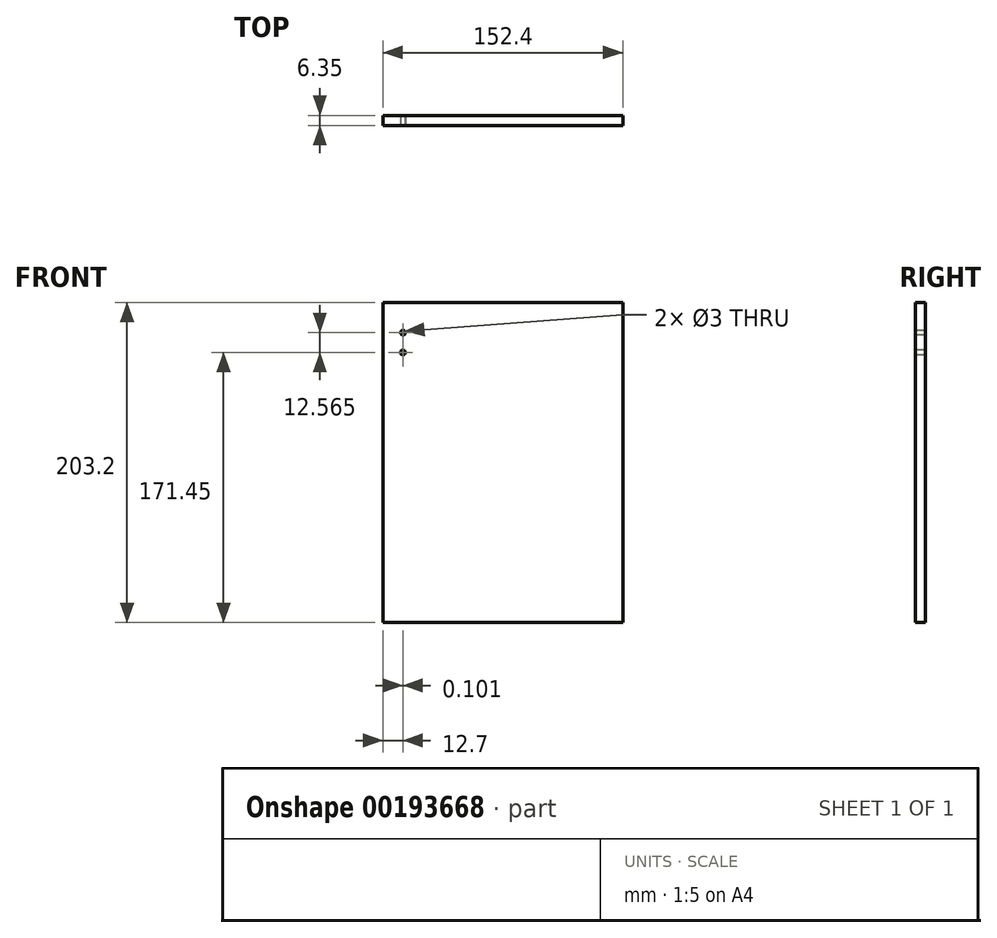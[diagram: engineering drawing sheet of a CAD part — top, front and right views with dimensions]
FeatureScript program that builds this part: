
annotation { "Feature Type Name" : "Feature", "Feature Type Description" : "" }
export const myFeature = defineFeature(function(context is Context, id is Id, definition is map)
    precondition{}
    {
        {
            var Q0;
            Q0=qCreatedBy(makeId("Front.planeOp"),FACE);
            var sketch = newSketch(context, id + "F0", { "sketchPlane" : qUnion([Q0])});
            skLineSegment(sketch, "E0.bottom", {"start": v(-76.2, -101.6) * mm, "end": v(76.2, -101.6) * mm});
            skLineSegment(sketch, "E0.top", {"start": v(-76.2, 101.6) * mm, "end": v(76.2, 101.6) * mm});
            skLineSegment(sketch, "E0.left", {"start": v(-76.2, -101.6) * mm, "end": v(-76.2, 101.6) * mm});
            skLineSegment(sketch, "E0.right", {"start": v(76.2, -101.6) * mm, "end": v(76.2, 101.6) * mm});
            skPoint(sketch, "E0.middle", {"position": v(0, 0) * mm});
            skSolve(sketch);
        }
        {
            var Q0;
            Q0=makeQuery(id+"F0.imprint","IMPRINT",FACE,{"disambiguationData":[TD([[makeQuery(id+"F0.imprint","IMPRINT",EDGE,{"derivedFrom":sQuery(id+"F0.wireOp",EDGE,"E0.bottom")}),1.0]])]});
            extrude(context, id + "F1", {"entities" : qUnion([Q0]), "oppositeDirection" : true, "depth" : 6.35 * mm});
        }
        {
            var Q0;
            Q0=makeQuery(id+"F1.opExtrude","CAP_FACE",FACE,{"disambiguationData":[OSD([sQuery(id+"F0.wireOp",EDGE,"E0.bottom"),sQuery(id+"F0.wireOp",EDGE,"E0.top"),sQuery(id+"F0.wireOp",EDGE,"E0.left"),sQuery(id+"F0.wireOp",EDGE,"E0.right")])],"isStart":true});
            var sketch = newSketch(context, id + "F2", { "sketchPlane" : qUnion([Q0])});
            skLineSegment(sketch, "E1", {"start": v(-63.5, 101.6) * mm, "end": v(-63.5, 82.55) * mm});
            skLineSegment(sketch, "E2", {"start": v(-63.5, 82.55) * mm, "end": v(-63.5, 69.85) * mm});
            skCircle(sketch, "E3", {"center": v(-63.4, 82.41) * mm, "radius": 1.5 * mm});
            skCircle(sketch, "E4", {"center": v(-63.5, 69.85) * mm, "radius": 1.5 * mm});
            skSolve(sketch);
        }
        {
            var Q0;
            {var subQ0=sQuery(id+"F2.wireOp",EDGE,"E2");var subQ1=sQuery(id+"F2.wireOp",EDGE,"E1");var subQ2=makeQuery(id+"F2.imprint","INTERSECT",VERTEX,{"derivedFrom":[subQ1,subQ0]});Q0=makeQuery(id+"F2.imprint","IMPRINT",FACE,{"disambiguationData":[TD([[makeQuery(id+"F2.imprint","IMPRINT",EDGE,{"disambiguationData":[TD([[subQ2,1.0]])],"derivedFrom":subQ1}),-1.0]])]});}
            var Q1;
            Q1=makeQuery(id+"F2.imprint","IMPRINT",FACE,{"disambiguationData":[TD([[makeQuery(id+"F2.imprint","IMPRINT",EDGE,{"derivedFrom":sQuery(id+"F2.wireOp",EDGE,"E4")}),1.0]])]});
            var Q2;
            {var subQ0=sQuery(id+"F2.wireOp",EDGE,"E2");var subQ1=sQuery(id+"F2.wireOp",EDGE,"E1");var subQ2=makeQuery(id+"F2.imprint","INTERSECT",VERTEX,{"derivedFrom":[subQ1,subQ0]});Q2=makeQuery(id+"F2.imprint","IMPRINT",FACE,{"disambiguationData":[TD([[makeQuery(id+"F2.imprint","IMPRINT",EDGE,{"disambiguationData":[TD([[subQ2,1.0]])],"derivedFrom":subQ1}),1.0]])]});}
            extrude(context, id + "F3", {"entities" : qUnion([Q0, Q1, Q2]), "operationType" : NewBodyOperationType.REMOVE, "oppositeDirection" : true, "depth" : 12.7 * mm});
        }
    });
